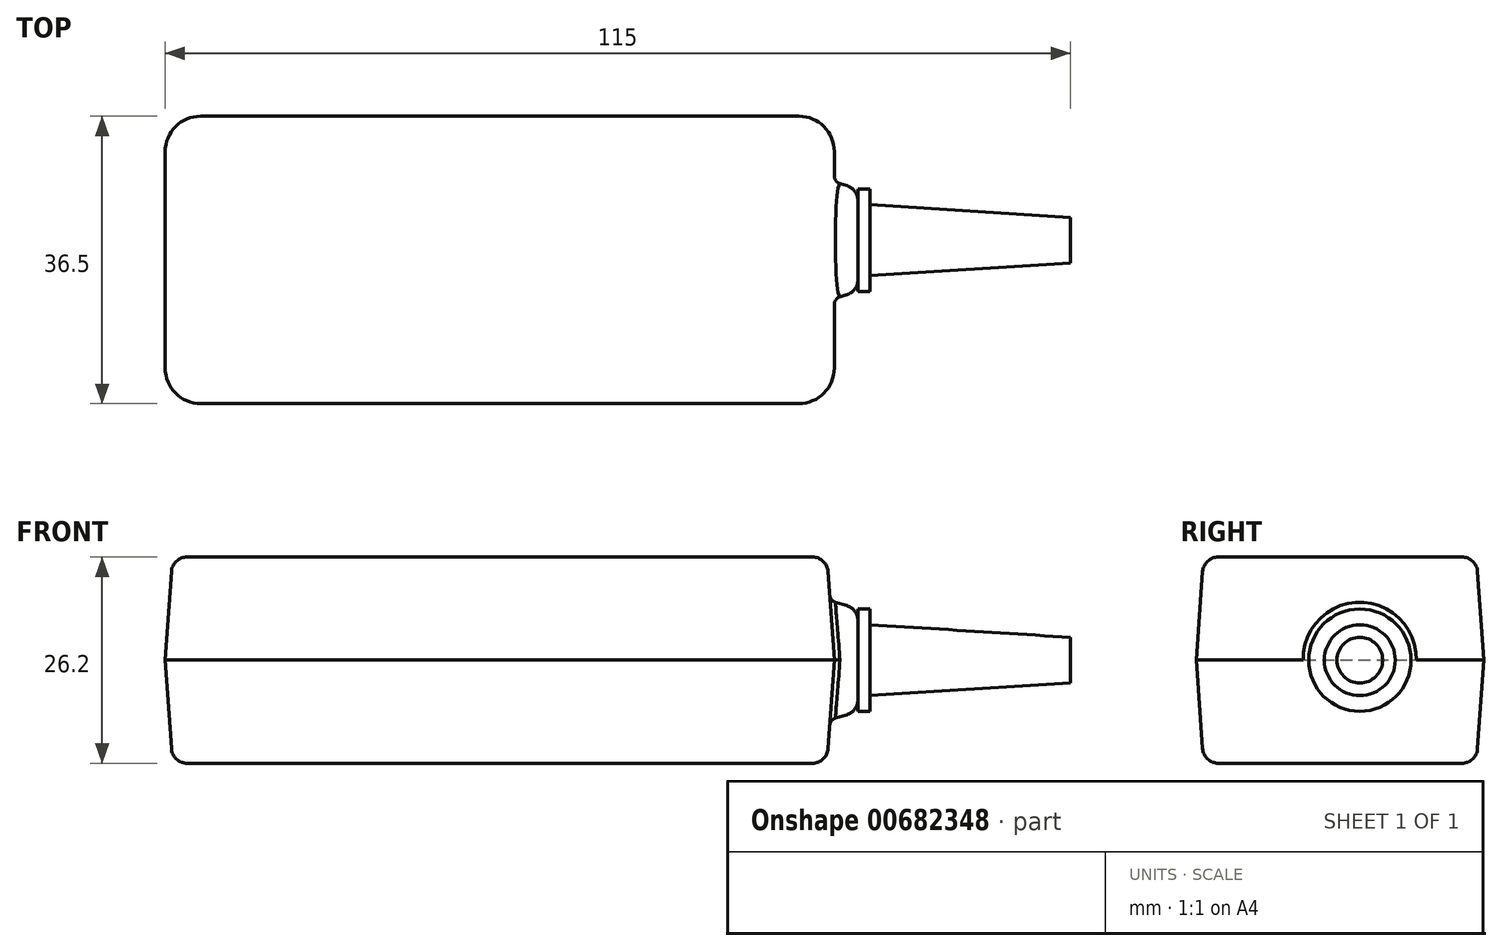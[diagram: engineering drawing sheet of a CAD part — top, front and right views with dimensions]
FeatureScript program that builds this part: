
annotation { "Feature Type Name" : "Feature", "Feature Type Description" : "" }
export const myFeature = defineFeature(function(context is Context, id is Id, definition is map)
    precondition{}
    {
        {
            var Q0;
            Q0=qCreatedBy(makeId("Top.planeOp"),FACE);
            var sketch = newSketch(context, id + "F0", { "sketchPlane" : qUnion([Q0])});
            skArc(sketch, "E0", {"start": v(0, 13.75) * mm, "mid": v(-1.32, 16.93) * mm, "end": v(-4.5, 18.25) * mm});
            skArc(sketch, "E1", {"start": v(-4.5, -18.25) * mm, "mid": v(-1.32, -16.93) * mm, "end": v(0, -13.75) * mm});
            skArc(sketch, "E2", {"start": v(-85, -13.75) * mm, "mid": v(-83.68, -16.93) * mm, "end": v(-80.5, -18.25) * mm});
            skArc(sketch, "E3", {"start": v(-80.5, 18.25) * mm, "mid": v(-83.68, 16.93) * mm, "end": v(-85, 13.75) * mm});
            skLineSegment(sketch, "E4", {"start": v(0, 13.75) * mm, "end": v(0, -13.75) * mm});
            skLineSegment(sketch, "E5", {"start": v(-4.5, 18.25) * mm, "end": v(-80.5, 18.25) * mm});
            skLineSegment(sketch, "E6", {"start": v(-85, 13.75) * mm, "end": v(-85, -13.75) * mm});
            skLineSegment(sketch, "E7", {"start": v(-4.5, -18.25) * mm, "end": v(-80.5, -18.25) * mm});
            skSolve(sketch);
        }
        {
            var Q0;
            Q0=makeQuery(id+"F0.imprint","IMPRINT",FACE,{"disambiguationData":[TD([[makeQuery(id+"F0.imprint","IMPRINT",EDGE,{"derivedFrom":sQuery(id+"F0.wireOp",EDGE,"E0")}),1.0]])]});
            extrude(context, id + "F1", {"entities" : qUnion([Q0]), "endBound" : BoundingType.SYMMETRIC, "depth" : 26.2 * mm, "offsetDistance" : 25 * mm, "hasDraft" : true, "draftAngle" : 4 * degree, "draftPullDirection" : true});
        }
        {
            var Q0;
            Q0=qCreatedBy(makeId("Top.planeOp"),FACE);
            var sketch = newSketch(context, id + "F2", { "sketchPlane" : qUnion([Q0])});
            skLineSegment(sketch, "E8", {"start": v(-2, 10.5) * mm, "end": v(3, 9) * mm});
            skLineSegment(sketch, "E9", {"start": v(3, 9) * mm, "end": v(3, -4) * mm});
            skLineSegment(sketch, "E10", {"start": v(3, -4) * mm, "end": v(-2, -5.5) * mm});
            skLineSegment(sketch, "E11", {"start": v(-2, -5.5) * mm, "end": v(-2, 10.5) * mm});
            skLineSegment(sketch, "E12", {"start": v(-2, 2.5) * mm, "end": v(3, 2.5) * mm});
            skLineSegment(sketch, "E13", {"start": v(3, 9) * mm, "end": v(4.5, 9) * mm});
            skLineSegment(sketch, "E14", {"start": v(4.5, 9) * mm, "end": v(4.5, -4) * mm});
            skLineSegment(sketch, "E15", {"start": v(4.5, -4) * mm, "end": v(3, -4) * mm});
            skLineSegment(sketch, "E16", {"start": v(3, 2.5) * mm, "end": v(30, 2.5) * mm});
            skLineSegment(sketch, "E17", {"start": v(30, 5.4) * mm, "end": v(30, -0.4) * mm});
            skLineSegment(sketch, "E18", {"start": v(30, 5.4) * mm, "end": v(4.5, 7) * mm});
            skSolve(sketch);
        }
        {
            var Q0;
            {var subQ0=sQuery(id+"F2.wireOp",EDGE,"E8");Q0=makeQuery(id+"F2.imprint","IMPRINT",FACE,{"disambiguationData":[TD([[makeQuery(id+"F2.imprint","IMPRINT",EDGE,{"derivedFrom":subQ0}),-1.0]])]});}
            var Q1;
            Q1=sQuery(id+"F2.wireOp",EDGE,"E12");
            revolve(context, id + "F3", {"operationType" : NewBodyOperationType.ADD, "entities" : qUnion([Q0]), "axis" : qUnion([Q1]), "revolveType" : RevolveType.FULL});
        }
        {
            var Q0;
            Q0=makeQuery(id+"F1.opExtrude","CAP_FACE",FACE,{"disambiguationData":[OSD([sQuery(id+"F0.wireOp",EDGE,"E0"),sQuery(id+"F0.wireOp",EDGE,"E1"),sQuery(id+"F0.wireOp",EDGE,"E2"),sQuery(id+"F0.wireOp",EDGE,"E3"),sQuery(id+"F0.wireOp",EDGE,"E4"),sQuery(id+"F0.wireOp",EDGE,"E5"),sQuery(id+"F0.wireOp",EDGE,"E6"),sQuery(id+"F0.wireOp",EDGE,"E7")])],"isStart":false});
            var Q1;
            Q1=makeQuery(id+"F1.opExtrude","CAP_FACE",FACE,{"disambiguationData":[OSD([sQuery(id+"F0.wireOp",EDGE,"E0"),sQuery(id+"F0.wireOp",EDGE,"E1"),sQuery(id+"F0.wireOp",EDGE,"E2"),sQuery(id+"F0.wireOp",EDGE,"E3"),sQuery(id+"F0.wireOp",EDGE,"E4"),sQuery(id+"F0.wireOp",EDGE,"E5"),sQuery(id+"F0.wireOp",EDGE,"E6"),sQuery(id+"F0.wireOp",EDGE,"E7")])],"isStart":true});
            var Q2;
            Q2=makeQuery(id+"F3.opRevolve","SWEPT_FACE",FACE,{"disambiguationData":[OSD([sQuery(id+"F2.wireOp",EDGE,"E9")])]});
            fillet(context, id + "F4", {"entities" : qUnion([Q0, Q1, Q2]), "radius" : 2 * mm, "tangentPropagation" : true, "allowEdgeOverflow" : false});
        }
        {
            var Q0;
            Q0=makeQuery(id+"F3.boolean.opBoolean","INTERSECT",EDGE,{"derivedFrom":[makeQuery(id+"F1.*.split.splitOp","SPLIT",FACE,{"derivedFrom":makeQuery(id+"F1.opExtrude","SWEPT_FACE",FACE,{"disambiguationData":[OSD([sQuery(id+"F0.wireOp",EDGE,"E4")])]})}),makeQuery(id+"F3.opRevolve","SWEPT_FACE",FACE,{"disambiguationData":[OSD([sQuery(id+"F2.wireOp",EDGE,"E8")])]})]});
            var Q1;
            Q1=makeQuery(id+"F3.boolean.opBoolean","INTERSECT",EDGE,{"derivedFrom":[makeQuery(id+"F1.*.split.splitOp","SPLIT",FACE,{"derivedFrom":makeQuery(id+"F1.opExtrude","SWEPT_FACE",FACE,{"disambiguationData":[OSD([sQuery(id+"F0.wireOp",EDGE,"E4")])]}),"isFromBackBody":true}),makeQuery(id+"F3.opRevolve","SWEPT_FACE",FACE,{"disambiguationData":[OSD([sQuery(id+"F2.wireOp",EDGE,"E8")])]})]});
            fillet(context, id + "F5", {"entities" : qUnion([Q0, Q1]), "radius" : 1 * mm, "tangentPropagation" : true, "allowEdgeOverflow" : false});
        }
        {
            var Q0;
            {var subQ4=sQuery(id+"F2.wireOp",EDGE,"E13");Q0=makeQuery(id+"F2.imprint","IMPRINT",FACE,{"disambiguationData":[TD([[makeQuery(id+"F2.imprint","IMPRINT",EDGE,{"derivedFrom":subQ4}),-1.0]])]});}
            var Q1;
            {var subQ0=sQuery(id+"F2.wireOp",EDGE,"E18");Q1=makeQuery(id+"F2.imprint","IMPRINT",FACE,{"disambiguationData":[TD([[makeQuery(id+"F2.imprint","IMPRINT",EDGE,{"derivedFrom":subQ0}),1.0]])]});}
            var Q2;
            Q2=sQuery(id+"F2.wireOp",EDGE,"E16");
            revolve(context, id + "F6", {"entities" : qUnion([Q0, Q1]), "axis" : qUnion([Q2]), "revolveType" : RevolveType.FULL});
        }
    });
